FCSTD DOCUMENT  (FreeCAD 0.21R33771 (Git))
Label: Model_1
License: All rights reserved
LicenseURL: https://en.wikipedia.org/wiki/All_rights_reserved
objects: Sketcher::SketchObject×2, App::FeaturePython×2, Spreadsheet::Sheet×1, App::DocumentObjectGroupPython×1
note: 2 computed .brp shape members not serialized (recipe doc carries the construction recipe); baked Part::Feature solids carry a one-line shape summary decoded from their .brp

FEATURE [Spreadsheet::Sheet] Spreadsheet  label="Parametry"
  cells = A1='Parametry palca pacjenta, wartości proszę wpisywać w milimetrach; A3='Proszę wrowadzić średnicę palca pacjenta; B3='Średnica palca; C3(Srednica)=20; A4='Proszę wprowadzić długość palca pacjenta; B4='Długość palca; C4(Dlugosc)=80
FEATURE [Sketcher::SketchObject] Sketch001  label="Model_zgrzewania"
  FullyConstrained = true
  expr: Constraints[7] = <<Parametry>>.Dlugosc - 4
  expr: Constraints[8] = <<Parametry>>.Srednica * 1.25
  expr: Constraints[9] = <<Parametry>>.Srednica * 1.5 / 2
  sketch-geometry (3):
    g0: LineSegment StartX=78 StartY=25 StartZ=0 EndX=78 EndY=10 EndZ=0
    g1: LineSegment StartX=78 StartY=10 StartZ=0 EndX=2 EndY=10 EndZ=0
    g2: LineSegment StartX=2 StartY=10 StartZ=0 EndX=2 EndY=25 EndZ=0
  constraints (10):
    c: Coincident(g0,g1)
    c: Coincident(g1,g2)
    c: Horizontal(g1)
    c: Vertical(g0)
    c: Vertical(g2)
    c: DistanceX(g-1,g2) = 2
    c: Equal(g2,g0)
    c: DistanceX(g1,g1) = 76
    c: DistanceY(g-1,g2) = 25
    c: DistanceY(g2,g2) = 15
FEATURE [App::FeaturePython] Layer001  label="Zgrzewanie"  # WARN: FeaturePython — macro-defined, semantics opaque (R4)
  Group = -> [Sketch001]
FEATURE [Sketcher::SketchObject] Sketch  label="Model_cięcia"
  FullyConstrained = true
  expr: Constraints[10] = <<Parametry>>.Srednica * 2.5
  expr: Constraints[9] = <<Parametry>>.Dlugosc
  sketch-geometry (4):
    g0: LineSegment StartX=0 StartY=0 StartZ=0 EndX=80 EndY=0 EndZ=0
    g1: LineSegment StartX=80 StartY=0 StartZ=0 EndX=80 EndY=50 EndZ=0
    g2: LineSegment StartX=80 StartY=50 StartZ=0 EndX=0 EndY=50 EndZ=0
    g3: LineSegment StartX=0 StartY=50 StartZ=0 EndX=0 EndY=0 EndZ=0
  constraints (11):
    c: Coincident(g0,g1)
    c: Coincident(g1,g2)
    c: Coincident(g2,g3)
    c: Coincident(g3,g0)
    c: Horizontal(g0)
    c: Horizontal(g2)
    c: Vertical(g1)
    c: Vertical(g3)
    c: Coincident(g0,g-1)
    c: DistanceX(g0,g0) = 80
    c: DistanceY(g1,g1) = 50
FEATURE [App::FeaturePython] Layer  label="Cięcie laserem"  # WARN: FeaturePython — macro-defined, semantics opaque (R4)
  Group = -> [Sketch]
FEATURE [App::DocumentObjectGroupPython] LayerContainer  label="Warstwy"  # scripted group (container) (typed FeaturePython)
  Group = -> [Layer,Layer001]
